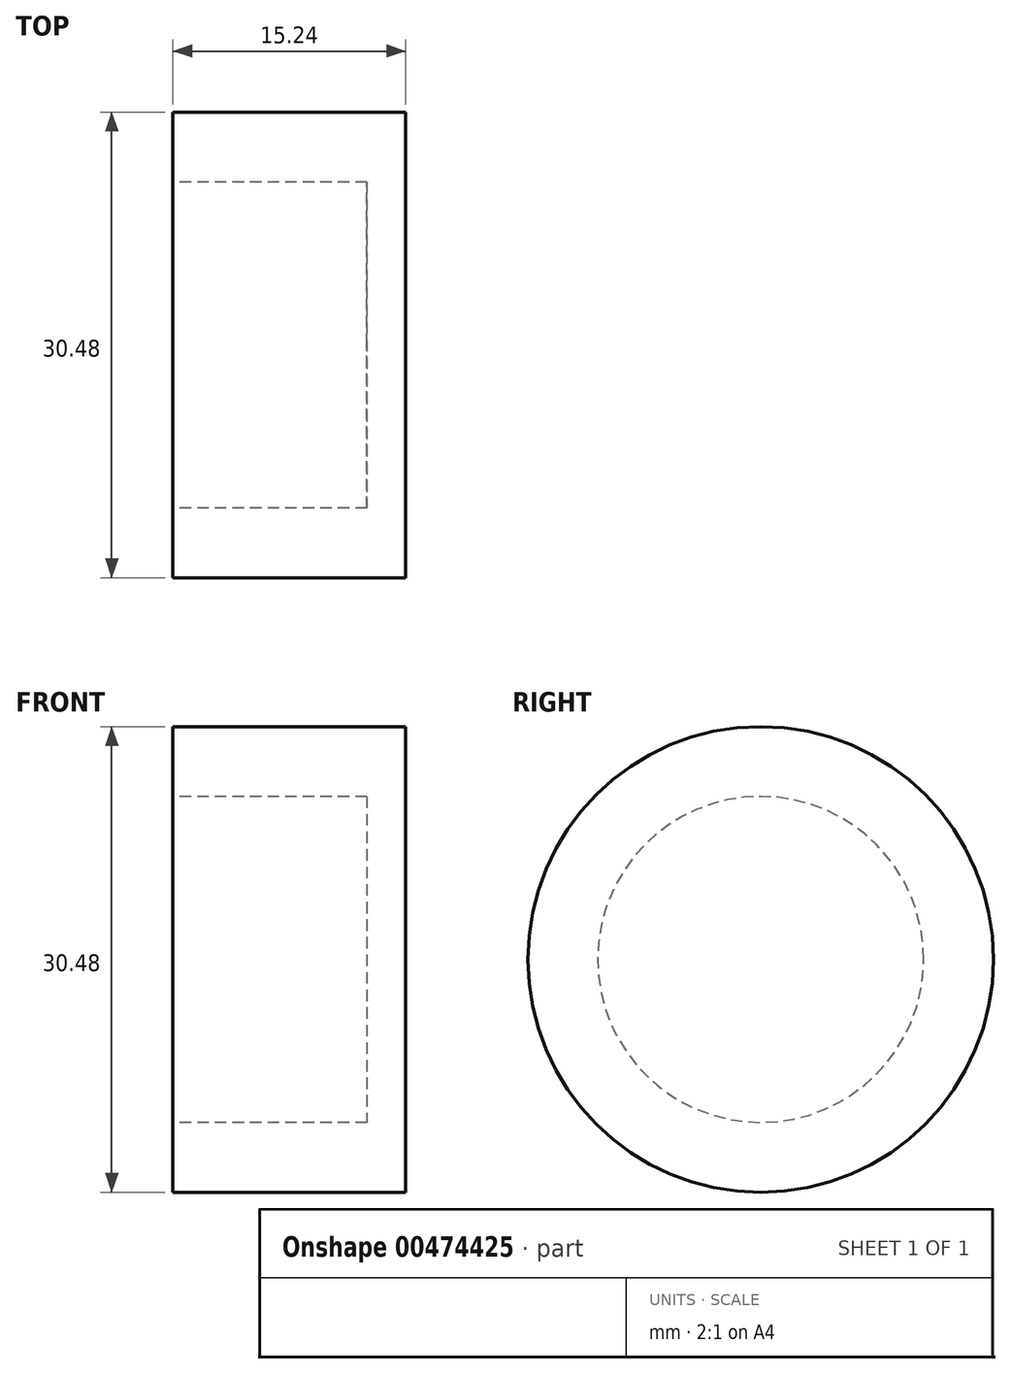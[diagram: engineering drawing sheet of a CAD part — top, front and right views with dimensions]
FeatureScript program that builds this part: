
annotation { "Feature Type Name" : "Feature", "Feature Type Description" : "" }
export const myFeature = defineFeature(function(context is Context, id is Id, definition is map)
    precondition{}
    {
        {
            var Q0;
            Q0=qCreatedBy(makeId("Front.planeOp"),FACE);
            var sketch = newSketch(context, id + "F0", { "sketchPlane" : qUnion([Q0])});
            skLineSegment(sketch, "E0.bottom", {"start": v(0, 0) * mm, "end": v(15.24, 0) * mm});
            skLineSegment(sketch, "E0.top", {"start": v(0, 15.24) * mm, "end": v(15.24, 15.24) * mm});
            skLineSegment(sketch, "E0.left", {"start": v(0, 0) * mm, "end": v(0, 15.24) * mm});
            skLineSegment(sketch, "E0.right", {"start": v(15.24, 0) * mm, "end": v(15.24, 15.24) * mm});
            skLineSegment(sketch, "E1.bottom", {"start": v(15.24, 0) * mm, "end": v(15.24, 0) * mm});
            skLineSegment(sketch, "E1.top", {"start": v(15.24, 15.24) * mm, "end": v(15.24, 15.24) * mm});
            skSolve(sketch);
        }
        {
            var Q0;
            Q0=makeQuery(id+"F0.imprint","IMPRINT",FACE,{"disambiguationData":[TD([[makeQuery(id+"F0.imprint","IMPRINT",EDGE,{"derivedFrom":sQuery(id+"F0.wireOp",EDGE,"E0.bottom")}),1.0]])]});
            var Q1;
            Q1=sQuery(id+"F0.wireOp",EDGE,"E0.bottom");
            revolve(context, id + "F1", {"entities" : qUnion([Q0]), "axis" : qUnion([Q1]), "revolveType" : RevolveType.FULL});
        }
        {
            var Q0;
            Q0=makeQuery(id+"F1.opRevolve","SWEPT_FACE",FACE,{"disambiguationData":[OSD([sQuery(id+"F0.wireOp",EDGE,"E0.left")])]});
            var sketch = newSketch(context, id + "F2", { "sketchPlane" : qUnion([Q0])});
            skCircle(sketch, "E2", {"center": v(0, 0) * mm, "radius": 10.67 * mm});
            skSolve(sketch);
        }
        {
            var Q0;
            Q0 = qSketchRegion(id + "F2", true);
            extrude(context, id + "F3", {"entities" : qUnion([Q0]), "operationType" : NewBodyOperationType.REMOVE, "oppositeDirection" : true, "depth" : 12.7 * mm});
        }
    });
